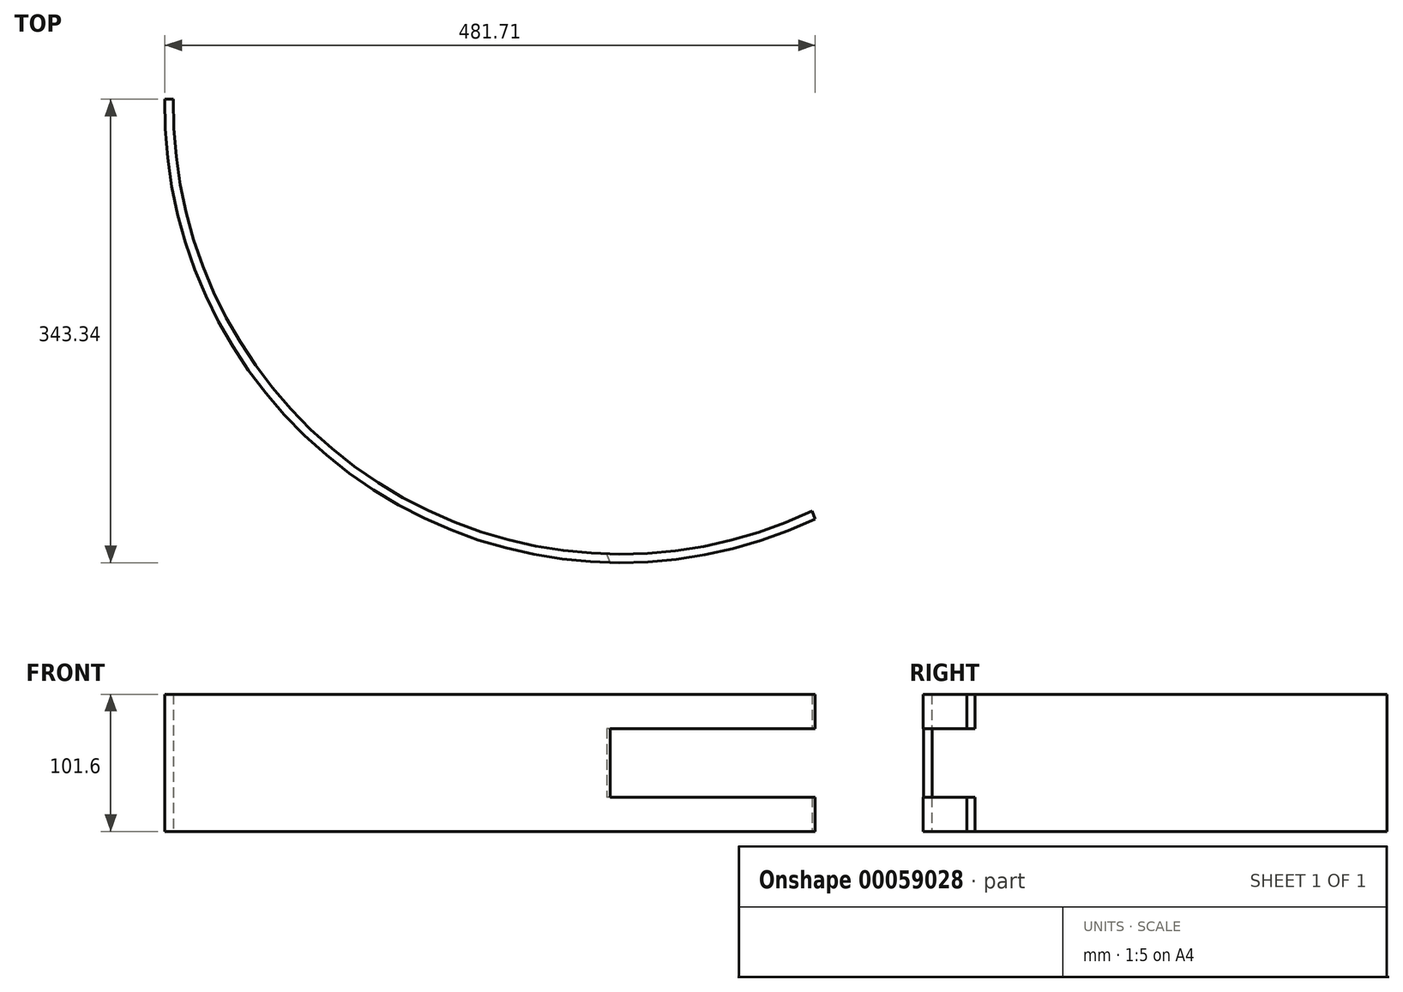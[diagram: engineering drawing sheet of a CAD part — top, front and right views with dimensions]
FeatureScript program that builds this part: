
annotation { "Feature Type Name" : "Feature", "Feature Type Description" : "" }
export const myFeature = defineFeature(function(context is Context, id is Id, definition is map)
    precondition{}
    {
        {
            var Q0;
            Q0=qCreatedBy(makeId("Top.planeOp"),FACE);
            var sketch = newSketch(context, id + "F0", { "sketchPlane" : qUnion([Q0])});
            skArc(sketch, "E0", {"start": v(0.03, 304.8) * mm, "mid": v(139.58, 2.42) * mm, "end": v(471.42, -25.71) * mm});
            skArc(sketch, "E1.0", {"start": v(-6.35, 304.8) * mm, "mid": v(136.07, -2.88) * mm, "end": v(473.9, -31.56) * mm});
            skLineSegment(sketch, "E2", {"start": v(471.42, -25.71) * mm, "end": v(473.9, -31.56) * mm});
            skLineSegment(sketch, "E3", {"start": v(-6.35, 304.8) * mm, "end": v(0.03, 304.8) * mm});
            skLineSegment(sketch, "E4", {"start": v(254.87, -101.88) * mm, "end": v(257.4, -107.84) * mm});
            skLineSegment(sketch, "E5", {"start": v(-147.23, 194.8) * mm, "end": v(-140.86, 194.8) * mm});
            skLineSegment(sketch, "E6", {"start": v(457.9, -31.75) * mm, "end": v(396.62, 114.16) * mm, "construction": true});
            skSolve(sketch);
        }
        {
            var Q0;
            Q0=makeQuery(id+"F0.imprint","IMPRINT",FACE,{"disambiguationData":[TD([[makeQuery(id+"F0.imprint","IMPRINT",EDGE,{"derivedFrom":sQuery(id+"F0.wireOp",EDGE,"E0")}),-1.0]])]});
            extrude(context, id + "F1", {"entities" : qUnion([Q0]), "depth" : 101.6 * mm});
        }
        {
            var Q0;
            Q0=makeQuery(id+"F1.opExtrude","SWEPT_FACE",FACE,{"disambiguationData":[OSD([sQuery(id+"F0.wireOp",EDGE,"E2")])]});
            var sketch = newSketch(context, id + "F2", { "sketchPlane" : qUnion([Q0])});
            skLineSegment(sketch, "E7.bottom", {"start": v(-316.85, 76.2) * mm, "end": v(-139.05, 76.2) * mm});
            skLineSegment(sketch, "E7.top", {"start": v(-316.85, 25.4) * mm, "end": v(-139.05, 25.4) * mm});
            skLineSegment(sketch, "E7.left", {"start": v(-316.85, 76.2) * mm, "end": v(-316.85, 25.4) * mm});
            skLineSegment(sketch, "E7.right", {"start": v(-139.05, 76.2) * mm, "end": v(-139.05, 25.4) * mm});
            skLineSegment(sketch, "E8", {"start": v(-214.23, 0) * mm, "end": v(-214.23, 25.4) * mm});
            skSolve(sketch);
        }
        {
            var Q0;
            Q0=qSketchRegion(id+"F2",true);
            extrude(context, id + "F3", {"entities" : qUnion([Q0]), "operationType" : NewBodyOperationType.REMOVE, "oppositeDirection" : true, "depth" : 152.4 * mm});
        }
        {
            var Q0;
            Q0=makeQuery(id+"F1.opExtrude","SWEPT_FACE",FACE,{"disambiguationData":[OSD([sQuery(id+"F0.wireOp",EDGE,"E3")])]});
            var sketch = newSketch(context, id + "F4", { "sketchPlane" : qUnion([Q0])});
            skLineSegment(sketch, "E9.bottom", {"start": v(55.66, -5.13) * mm, "end": v(-87.55, -5.13) * mm});
            skLineSegment(sketch, "E9.top", {"start": v(55.66, 113.42) * mm, "end": v(-87.55, 113.42) * mm});
            skLineSegment(sketch, "E9.left", {"start": v(55.66, -5.13) * mm, "end": v(55.66, 113.42) * mm});
            skLineSegment(sketch, "E9.right", {"start": v(-87.55, -5.13) * mm, "end": v(-87.55, 113.42) * mm});
            skSolve(sketch);
        }
        {
            var Q0;
            Q0=qSketchRegion(id+"F4",true);
            extrude(context, id + "F5", {"entities" : qUnion([Q0]), "operationType" : NewBodyOperationType.REMOVE, "oppositeDirection" : true, "depth" : 25.4 * mm});
        }
    });
